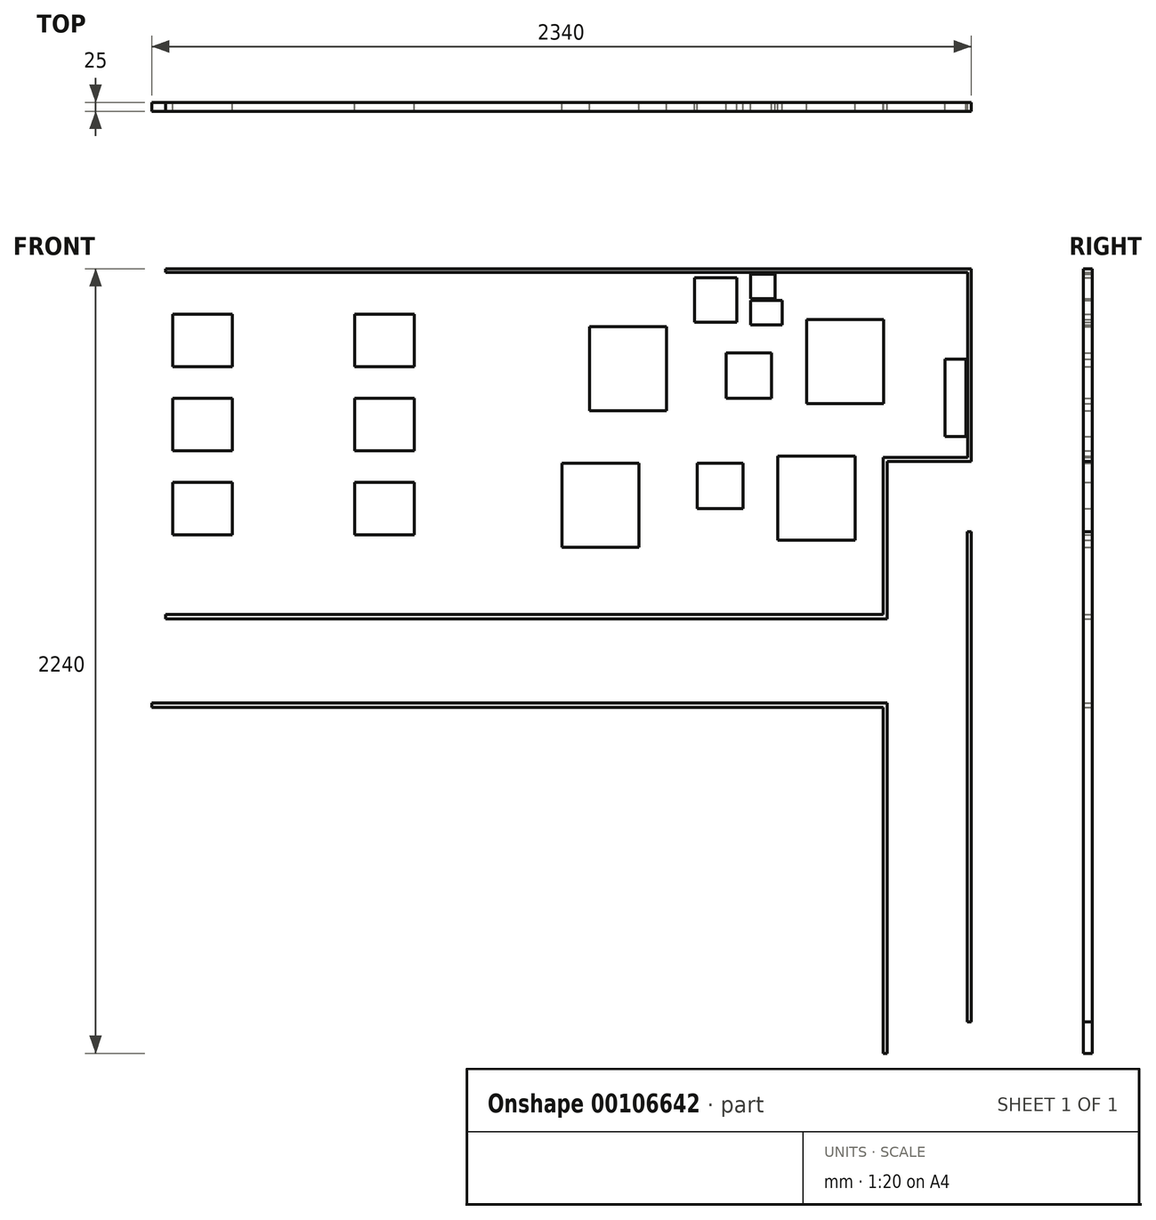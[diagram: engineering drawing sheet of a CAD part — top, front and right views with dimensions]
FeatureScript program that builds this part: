
annotation { "Feature Type Name" : "Feature", "Feature Type Description" : "" }
export const myFeature = defineFeature(function(context is Context, id is Id, definition is map)
    precondition{}
    {
        {
            var Q0;
            Q0=qCreatedBy(makeId("Front.planeOp"),FACE);
            var sketch = newSketch(context, id + "F0", { "sketchPlane" : qUnion([Q0])});
            skLineSegment(sketch, "E0.bottom", {"start": v(220, -120) * mm, "end": v(0, -120) * mm});
            skLineSegment(sketch, "E0.top", {"start": v(220, 120) * mm, "end": v(0, 120) * mm});
            skLineSegment(sketch, "E0.left", {"start": v(220, -120) * mm, "end": v(220, 120) * mm});
            skLineSegment(sketch, "E0.right", {"start": v(0, -120) * mm, "end": v(0, 120) * mm});
            skPoint(sketch, "E0.middle", {"position": v(110, 0) * mm});
            skLineSegment(sketch, "E1.bottom", {"start": v(470, 255) * mm, "end": v(-1830, 255) * mm});
            skLineSegment(sketch, "E1.top", {"start": v(470, 265) * mm, "end": v(-1830, 265) * mm});
            skLineSegment(sketch, "E1.left", {"start": v(470, 255) * mm, "end": v(470, 265) * mm});
            skLineSegment(sketch, "E1.right", {"start": v(-1830, 255) * mm, "end": v(-1830, 265) * mm});
            skLineSegment(sketch, "E2.bottom", {"start": v(-230, 25) * mm, "end": v(-100, 25) * mm});
            skLineSegment(sketch, "E2.top", {"start": v(-230, -105) * mm, "end": v(-100, -105) * mm});
            skLineSegment(sketch, "E2.left", {"start": v(-230, 25) * mm, "end": v(-230, -105) * mm});
            skLineSegment(sketch, "E2.right", {"start": v(-100, 25) * mm, "end": v(-100, -105) * mm});
            skLineSegment(sketch, "E3.bottom", {"start": v(-320, 240) * mm, "end": v(-200, 240) * mm});
            skLineSegment(sketch, "E3.top", {"start": v(-320, 113) * mm, "end": v(-200, 113) * mm});
            skLineSegment(sketch, "E3.left", {"start": v(-320, 240) * mm, "end": v(-320, 113) * mm});
            skLineSegment(sketch, "E3.right", {"start": v(-200, 240) * mm, "end": v(-200, 113) * mm});
            skLineSegment(sketch, "E4.bottom", {"start": v(-160, 175) * mm, "end": v(-70, 175) * mm});
            skLineSegment(sketch, "E4.top", {"start": v(-160, 105) * mm, "end": v(-70, 105) * mm});
            skLineSegment(sketch, "E4.left", {"start": v(-160, 175) * mm, "end": v(-160, 105) * mm});
            skLineSegment(sketch, "E4.right", {"start": v(-70, 175) * mm, "end": v(-70, 105) * mm});
            skLineSegment(sketch, "E5.bottom", {"start": v(-160, 250) * mm, "end": v(-90, 250) * mm});
            skLineSegment(sketch, "E5.top", {"start": v(-160, 180) * mm, "end": v(-90, 180) * mm});
            skLineSegment(sketch, "E5.left", {"start": v(-160, 250) * mm, "end": v(-160, 180) * mm});
            skLineSegment(sketch, "E5.right", {"start": v(-90, 250) * mm, "end": v(-90, 180) * mm});
            skLineSegment(sketch, "E6.bottom", {"start": v(-1830, -722.3) * mm, "end": v(230, -722.3) * mm});
            skLineSegment(sketch, "E6.top", {"start": v(-1830, -735) * mm, "end": v(230, -735) * mm});
            skLineSegment(sketch, "E6.left", {"start": v(-1830, -722.3) * mm, "end": v(-1830, -735) * mm});
            skLineSegment(sketch, "E6.right", {"start": v(470, -722.3) * mm, "end": v(470, -735) * mm});
            skLineSegment(sketch, "E7.bottom", {"start": v(470, 265) * mm, "end": v(460, 265) * mm});
            skLineSegment(sketch, "E7.left", {"start": v(470, 265) * mm, "end": v(470, -635) * mm});
            skLineSegment(sketch, "E7.right", {"start": v(460, 265) * mm, "end": v(460, -285.4) * mm});
            skLineSegment(sketch, "E8.bottom", {"start": v(395, 6.6) * mm, "end": v(455, 6.6) * mm});
            skLineSegment(sketch, "E8.top", {"start": v(395, -213.4) * mm, "end": v(455, -213.4) * mm});
            skLineSegment(sketch, "E8.left", {"start": v(395, 6.6) * mm, "end": v(395, -213.4) * mm});
            skLineSegment(sketch, "E8.right", {"start": v(455, 6.6) * mm, "end": v(455, -213.4) * mm});
            skLineSegment(sketch, "E9.bottom", {"start": v(-400, -140) * mm, "end": v(-620, -140) * mm});
            skLineSegment(sketch, "E9.top", {"start": v(-400, 100) * mm, "end": v(-620, 100) * mm});
            skLineSegment(sketch, "E9.left", {"start": v(-400, -140) * mm, "end": v(-400, 100) * mm});
            skLineSegment(sketch, "E9.right", {"start": v(-620, -140) * mm, "end": v(-620, 100) * mm});
            skLineSegment(sketch, "E10.bottom", {"start": v(-1290, 135) * mm, "end": v(-1120, 135) * mm});
            skLineSegment(sketch, "E10.top", {"start": v(-1290, -15) * mm, "end": v(-1120, -15) * mm});
            skLineSegment(sketch, "E10.left", {"start": v(-1290, 135) * mm, "end": v(-1290, -15) * mm});
            skLineSegment(sketch, "E10.right", {"start": v(-1120, 135) * mm, "end": v(-1120, -15) * mm});
            skLineSegment(sketch, "E11.bottom", {"start": v(-1290, -105) * mm, "end": v(-1120, -105) * mm});
            skLineSegment(sketch, "E11.top", {"start": v(-1290, -255) * mm, "end": v(-1120, -255) * mm});
            skLineSegment(sketch, "E11.left", {"start": v(-1290, -105) * mm, "end": v(-1290, -255) * mm});
            skLineSegment(sketch, "E11.right", {"start": v(-1120, -105) * mm, "end": v(-1120, -255) * mm});
            skLineSegment(sketch, "E12.bottom", {"start": v(230, -975) * mm, "end": v(-1870, -975) * mm});
            skLineSegment(sketch, "E12.top", {"start": v(230, -987) * mm, "end": v(-1870, -987) * mm});
            skLineSegment(sketch, "E12.left", {"start": v(230, -975) * mm, "end": v(230, -987) * mm});
            skLineSegment(sketch, "E12.right", {"start": v(-1870, -975) * mm, "end": v(-1870, -987) * mm});
            skLineSegment(sketch, "E13.bottom", {"start": v(230, -975) * mm, "end": v(218, -975) * mm});
            skLineSegment(sketch, "E13.top", {"start": v(230, -1975) * mm, "end": v(218, -1975) * mm});
            skLineSegment(sketch, "E13.left", {"start": v(230, -975) * mm, "end": v(230, -1975) * mm});
            skLineSegment(sketch, "E13.right", {"start": v(218, -975) * mm, "end": v(218, -1975) * mm});
            skLineSegment(sketch, "E14.bottom", {"start": v(-1810, 135) * mm, "end": v(-1640, 135) * mm});
            skLineSegment(sketch, "E14.top", {"start": v(-1810, -15) * mm, "end": v(-1640, -15) * mm});
            skLineSegment(sketch, "E14.left", {"start": v(-1810, 135) * mm, "end": v(-1810, -15) * mm});
            skLineSegment(sketch, "E14.right", {"start": v(-1640, 135) * mm, "end": v(-1640, -15) * mm});
            skLineSegment(sketch, "E15.bottom", {"start": v(-1810, -105) * mm, "end": v(-1640, -105) * mm});
            skLineSegment(sketch, "E15.top", {"start": v(-1810, -255) * mm, "end": v(-1640, -255) * mm});
            skLineSegment(sketch, "E15.left", {"start": v(-1810, -105) * mm, "end": v(-1810, -255) * mm});
            skLineSegment(sketch, "E15.right", {"start": v(-1640, -105) * mm, "end": v(-1640, -255) * mm});
            skLineSegment(sketch, "E16.bottom", {"start": v(230, -735) * mm, "end": v(218, -735) * mm});
            skLineSegment(sketch, "E16.top", {"start": v(230, -273.4) * mm, "end": v(218, -273.4) * mm});
            skLineSegment(sketch, "E16.left", {"start": v(230, -735) * mm, "end": v(230, -273.4) * mm});
            skLineSegment(sketch, "E16.right", {"start": v(218, -735) * mm, "end": v(218, -273.4) * mm});
            skLineSegment(sketch, "E17.bottom", {"start": v(218, -273.4) * mm, "end": v(470, -273.4) * mm});
            skLineSegment(sketch, "E17.top", {"start": v(218, -285.4) * mm, "end": v(470, -285.4) * mm});
            skLineSegment(sketch, "E17.left", {"start": v(218, -273.4) * mm, "end": v(218, -285.4) * mm});
            skLineSegment(sketch, "E17.right", {"start": v(470, -273.4) * mm, "end": v(470, -285.4) * mm});
            skLineSegment(sketch, "E18.bottom", {"start": v(138, -510) * mm, "end": v(-82, -510) * mm});
            skLineSegment(sketch, "E18.top", {"start": v(138, -270) * mm, "end": v(-82, -270) * mm});
            skLineSegment(sketch, "E18.left", {"start": v(138, -510) * mm, "end": v(138, -270) * mm});
            skLineSegment(sketch, "E18.right", {"start": v(-82, -510) * mm, "end": v(-82, -270) * mm});
            skLineSegment(sketch, "E19.bottom", {"start": v(-312, -290) * mm, "end": v(-182, -290) * mm});
            skLineSegment(sketch, "E19.top", {"start": v(-312, -420) * mm, "end": v(-182, -420) * mm});
            skLineSegment(sketch, "E19.left", {"start": v(-312, -290) * mm, "end": v(-312, -420) * mm});
            skLineSegment(sketch, "E19.right", {"start": v(-182, -290) * mm, "end": v(-182, -420) * mm});
            skLineSegment(sketch, "E20.bottom", {"start": v(-479, -530) * mm, "end": v(-699, -530) * mm});
            skLineSegment(sketch, "E20.top", {"start": v(-479, -290) * mm, "end": v(-699, -290) * mm});
            skLineSegment(sketch, "E20.left", {"start": v(-479, -530) * mm, "end": v(-479, -290) * mm});
            skLineSegment(sketch, "E20.right", {"start": v(-699, -530) * mm, "end": v(-699, -290) * mm});
            skLineSegment(sketch, "E21.bottom", {"start": v(458, -485.4) * mm, "end": v(470, -485.4) * mm});
            skLineSegment(sketch, "E21.top", {"start": v(458, -1885.4) * mm, "end": v(470, -1885.4) * mm});
            skLineSegment(sketch, "E21.left", {"start": v(458, -485.4) * mm, "end": v(458, -1885.4) * mm});
            skLineSegment(sketch, "E21.right", {"start": v(470, -485.4) * mm, "end": v(470, -1885.4) * mm});
            skLineSegment(sketch, "E22.bottom", {"start": v(-1290, -345) * mm, "end": v(-1120, -345) * mm});
            skLineSegment(sketch, "E22.top", {"start": v(-1290, -495) * mm, "end": v(-1120, -495) * mm});
            skLineSegment(sketch, "E22.left", {"start": v(-1290, -345) * mm, "end": v(-1290, -495) * mm});
            skLineSegment(sketch, "E22.right", {"start": v(-1120, -345) * mm, "end": v(-1120, -495) * mm});
            skLineSegment(sketch, "E23.bottom", {"start": v(-1810, -345) * mm, "end": v(-1640, -345) * mm});
            skLineSegment(sketch, "E23.top", {"start": v(-1810, -495) * mm, "end": v(-1640, -495) * mm});
            skLineSegment(sketch, "E23.left", {"start": v(-1810, -345) * mm, "end": v(-1810, -495) * mm});
            skLineSegment(sketch, "E23.right", {"start": v(-1640, -345) * mm, "end": v(-1640, -495) * mm});
            skSolve(sketch);
        }
        {
            var Q0;
            Q0=qSketchRegion(id+"F0",true);
            extrude(context, id + "F1", {"entities" : qUnion([Q0]), "depth" : 25 * mm});
        }
    });
